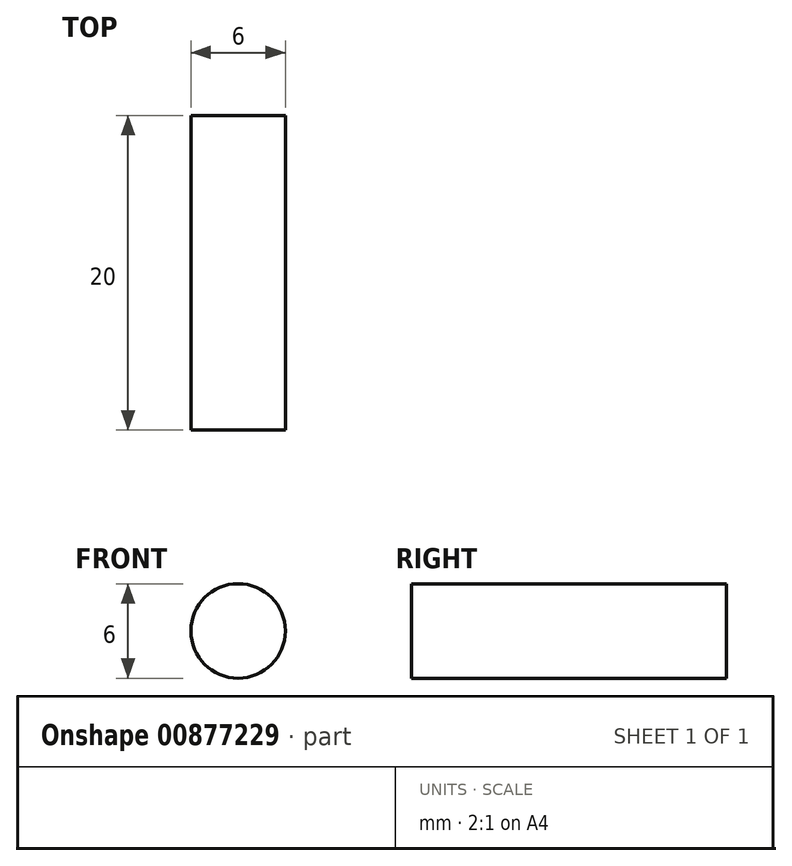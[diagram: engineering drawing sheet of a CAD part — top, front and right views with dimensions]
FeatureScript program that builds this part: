
annotation { "Feature Type Name" : "Feature", "Feature Type Description" : "" }
export const myFeature = defineFeature(function(context is Context, id is Id, definition is map)
    precondition{}
    {
        {
            var Q0;
            Q0=qCreatedBy(makeId("Front.planeOp"),FACE);
            var sketch = newSketch(context, id + "F0", { "sketchPlane" : qUnion([Q0])});
            skCircle(sketch, "E0", {"center": v(0, 0) * mm, "radius": 3 * mm});
            skSolve(sketch);
        }
        {
            var Q0;
            Q0 = qSketchRegion(id + "F0", true);
            extrude(context, id + "F1", {"entities" : qUnion([Q0]), "depth" : 20 * mm, "offsetDistance" : 25.4 * mm});
        }
    });
